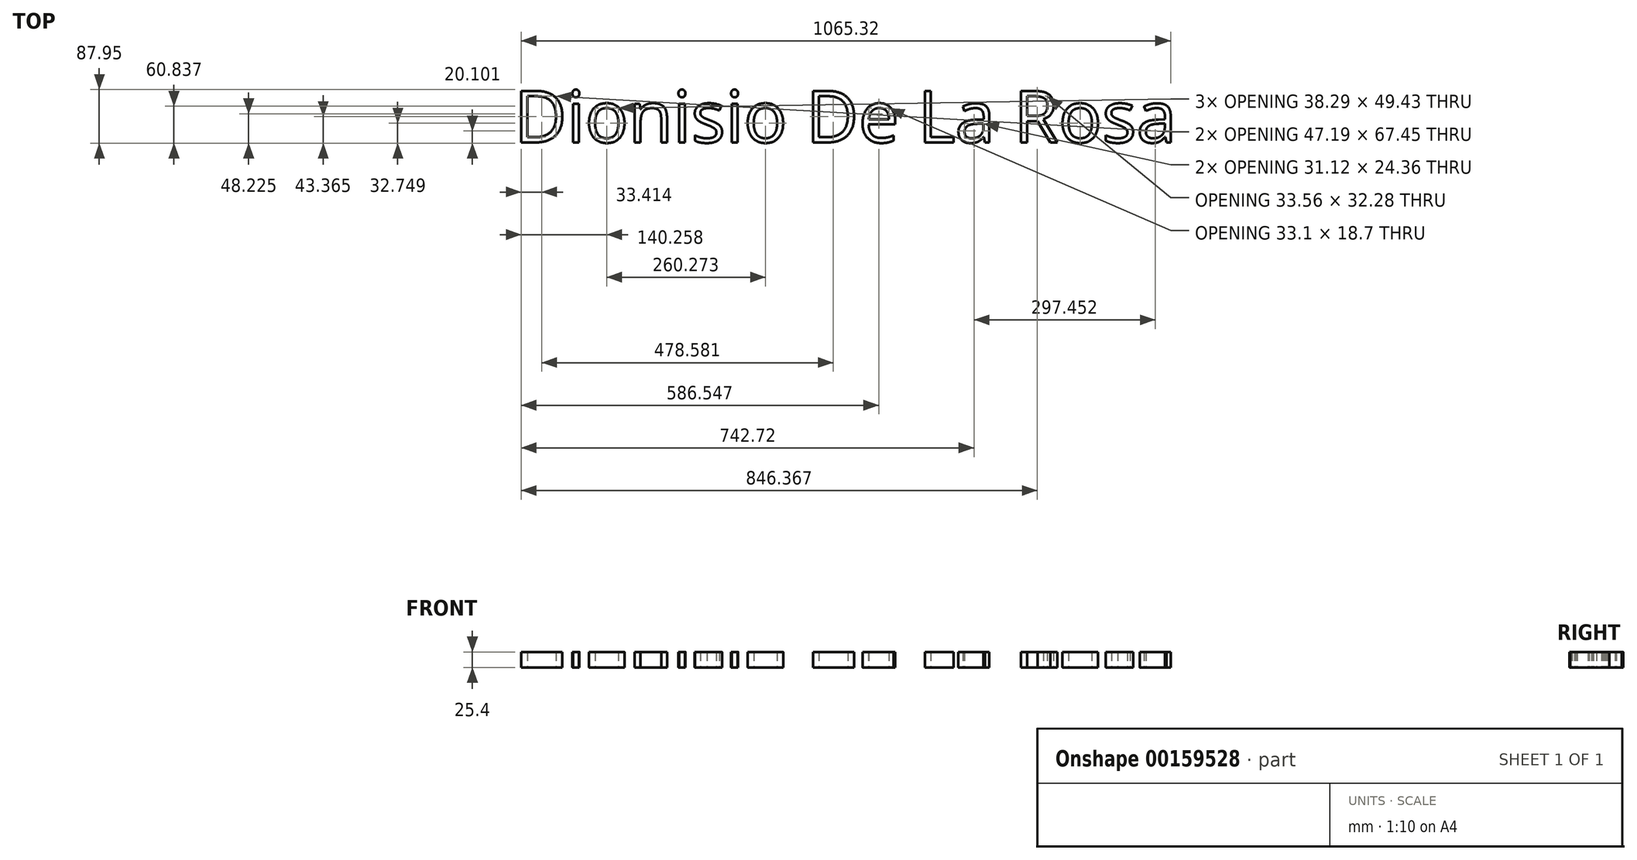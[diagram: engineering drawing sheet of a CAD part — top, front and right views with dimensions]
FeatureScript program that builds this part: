
annotation { "Feature Type Name" : "Feature", "Feature Type Description" : "" }
export const myFeature = defineFeature(function(context is Context, id is Id, definition is map)
    precondition{}
    {
        {
            var Q0;
            Q0=qCreatedBy(makeId("Top.planeOp"),FACE);
            var sketch = newSketch(context, id + "F0", { "sketchPlane" : qUnion([Q0])});
            skText(sketch, "E0", { "text": "Dionisio De La Rosa\n", "fontName": "OpenSans-Regular.ttf"});
            const initialGuessF0  = {"E0": [-0.39213, -0.02916, 1, 0, 0.08515]};
            skSetInitialGuess(sketch, initialGuessF0);
            skSolve(sketch);
        }
        {
            var Q0;
            Q0 = qSketchRegion(id + "F0", true);
            extrude(context, id + "F1", {"entities" : qUnion([Q0]), "depth" : 25.4 * mm});
        }
    });
